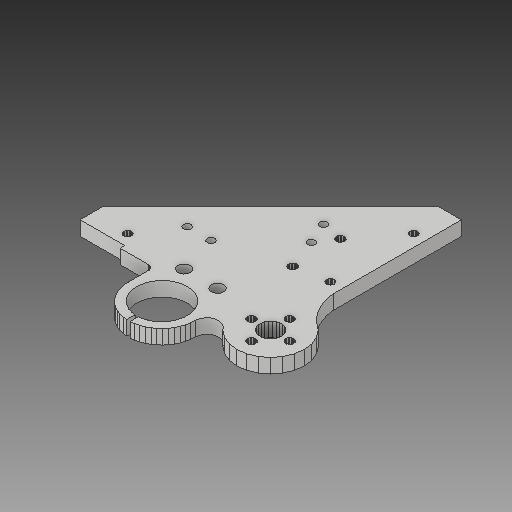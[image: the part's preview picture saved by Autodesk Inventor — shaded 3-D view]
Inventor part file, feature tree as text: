
AUTODESK INVENTOR PART (.ipt)
format: ipt  version: 2017 (Build 210142000, 142)  size: 541,696 bytes
history: native  units: mm
features: extrude x1, hole x1, sketch x1
ambient origin geometry x8: Origin, YZ Plane, XZ Plane, XY Plane, X Axis, Y Axis, Z Axis, Center Point
bodies: Solid1 (feature_tree)
feature tree (3):
  extrude  "Extrusion1"  [1 undecoded]
  hole  "Hole1"  [1 undecoded]
  sketch  "Sketch2"  dims[d0=6.0mm d1=0.0mm d2=21.2mm d3=6.0mm d4=4.0mm d5=2.0mm d6=90.0deg d7=8.0mm d8=20.594885mm]
note: 2 required parameter values undecoded (feature->parameter linkage not recoverable at this tier; creation-order binding heuristic only, values carry confidence <= 0.55)
